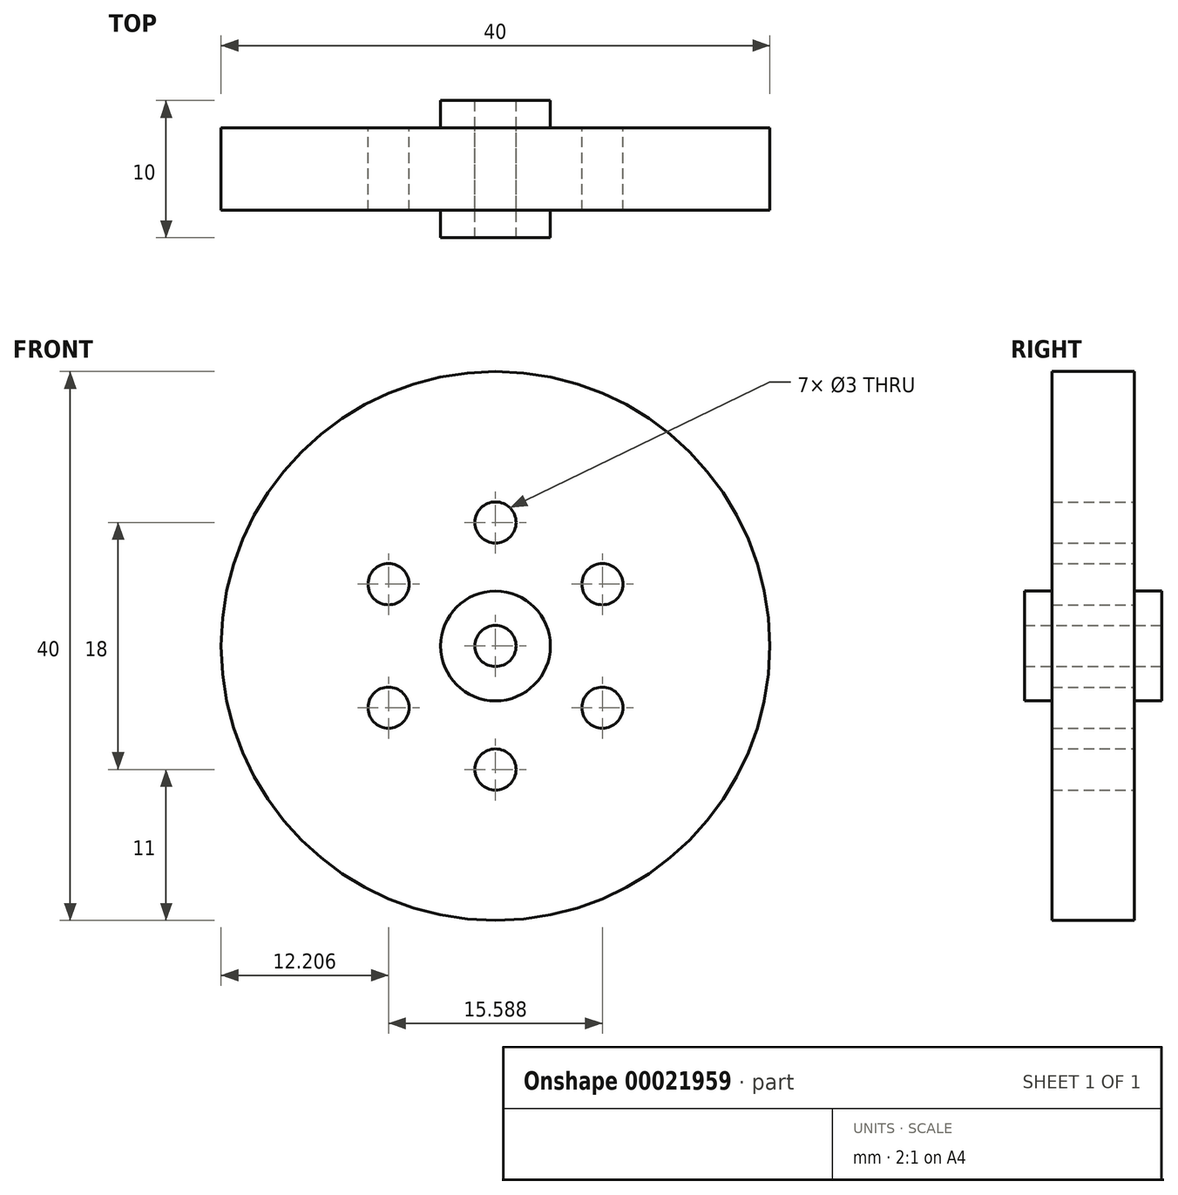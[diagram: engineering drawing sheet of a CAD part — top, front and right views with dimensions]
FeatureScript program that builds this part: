
annotation { "Feature Type Name" : "Feature", "Feature Type Description" : "" }
export const myFeature = defineFeature(function(context is Context, id is Id, definition is map)
    precondition{}
    {
        {
            var Q0;
            Q0=qCreatedBy(makeId("Front.planeOp"),FACE);
            var sketch = newSketch(context, id + "F0", { "sketchPlane" : qUnion([Q0])});
            skCircle(sketch, "E0", {"center": v(0, 0) * mm, "radius": 20 * mm});
            skCircle(sketch, "E1", {"center": v(0, 0) * mm, "radius": 1.5 * mm});
            skCircle(sketch, "E2", {"center": v(0, 9) * mm, "radius": 1.5 * mm});
            skCircle(sketch, "E3.1.0", {"center": v(-7.8, 4.5) * mm, "radius": 1.5 * mm});
            skCircle(sketch, "E3.2.0", {"center": v(-7.8, -4.5) * mm, "radius": 1.5 * mm});
            skCircle(sketch, "E3.3.0", {"center": v(0, -9) * mm, "radius": 1.5 * mm});
            skCircle(sketch, "E3.4.0", {"center": v(7.8, -4.5) * mm, "radius": 1.5 * mm});
            skCircle(sketch, "E3.5.0", {"center": v(7.8, 4.5) * mm, "radius": 1.5 * mm});
            skCircle(sketch, "E4", {"center": v(0, 0) * mm, "radius": 4 * mm});
            skSolve(sketch);
        }
        {
            var Q0;
            Q0=makeQuery(id+"F0.imprint","IMPRINT",FACE,{"disambiguationData":[TD([[makeQuery(id+"F0.imprint","IMPRINT",EDGE,{"derivedFrom":sQuery(id+"F0.wireOp",EDGE,"E0")}),1.0]])]});
            extrude(context, id + "F1", {"entities" : qUnion([Q0]), "depth" : 6 * mm});
        }
        {
            var Q0;
            Q0=makeQuery(id+"F0.imprint","IMPRINT",FACE,{"disambiguationData":[TD([[makeQuery(id+"F0.imprint","IMPRINT",EDGE,{"derivedFrom":sQuery(id+"F0.wireOp",EDGE,"E1")}),-1.0]])]});
            extrude(context, id + "F2", {"entities" : qUnion([Q0]), "operationType" : NewBodyOperationType.ADD, "depth" : 8 * mm});
        }
        {
            var Q0;
            Q0=makeQuery(id+"F0.imprint","IMPRINT",FACE,{"disambiguationData":[TD([[makeQuery(id+"F0.imprint","IMPRINT",EDGE,{"derivedFrom":sQuery(id+"F0.wireOp",EDGE,"E1")}),-1.0]])]});
            extrude(context, id + "F3", {"entities" : qUnion([Q0]), "operationType" : NewBodyOperationType.ADD, "oppositeDirection" : true, "depth" : 2 * mm});
        }
    });
